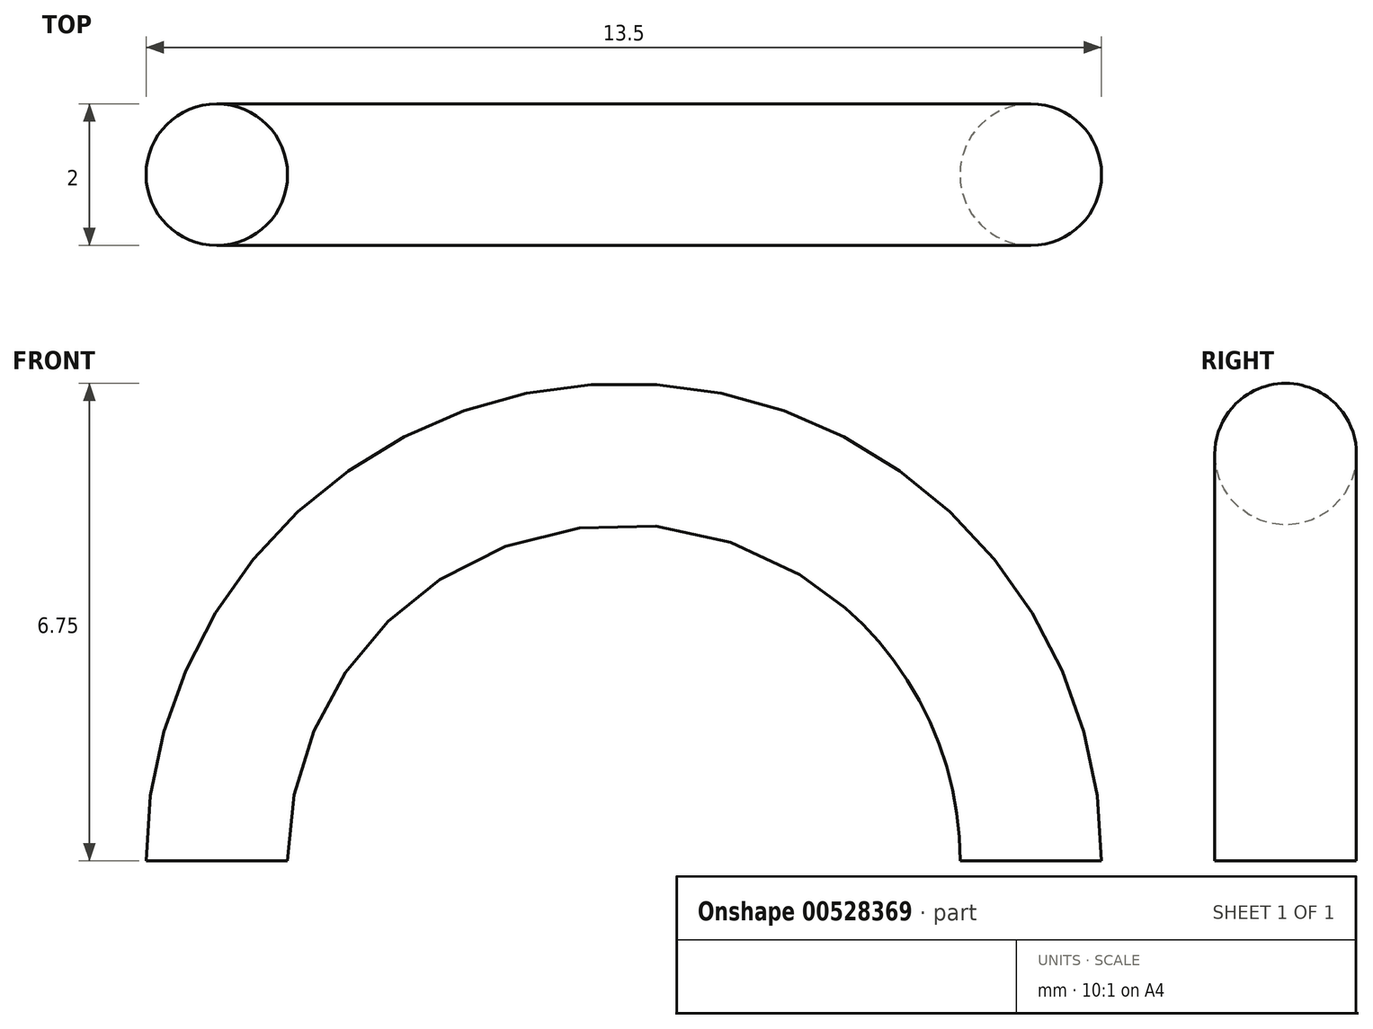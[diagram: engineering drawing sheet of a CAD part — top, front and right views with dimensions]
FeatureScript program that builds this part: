
annotation { "Feature Type Name" : "Feature", "Feature Type Description" : "" }
export const myFeature = defineFeature(function(context is Context, id is Id, definition is map)
    precondition{}
    {
        {
            var Q0;
            Q0=qCreatedBy(makeId("Front.planeOp"),FACE);
            var sketch = newSketch(context, id + "F0", { "sketchPlane" : qUnion([Q0])});
            skArc(sketch, "E0", {"start": v(11.5, 0) * mm, "mid": v(5.75, 5.75) * mm, "end": v(0, 0) * mm});
            skSolve(sketch);
        }
        {
            var Q0;
            Q0=sQuery(id+"F0.wireOp",EDGE,"E0");
            var Q1;
            Q1=sQuery(id+"F0.wireOp",VERTEX,"E0.start");
            cPlane(context, id + "F1", {"entities" : qUnion([Q0, Q1]), "cplaneType" : CPlaneType.CURVE_POINT, "offset" : 25.4 * mm, "width" : 152.4 * mm, "height" : 152.4 * mm});
        }
        {
            var Q0;
            Q0=qCreatedBy(id+"F1.planeOp",FACE);
            var sketch = newSketch(context, id + "F2", { "sketchPlane" : qUnion([Q0])});
            skCircle(sketch, "E1", {"center": v(11.5, 0) * mm, "radius": 1 * mm});
            skSolve(sketch);
        }
        {
            var Q0;
            Q0=makeQuery(id+"F2.imprint","IMPRINT",FACE,{"disambiguationData":[TD([[makeQuery(id+"F2.imprint","IMPRINT",EDGE,{"derivedFrom":sQuery(id+"F2.wireOp",EDGE,"E1")}),1.0]])]});
            var Q1;
            Q1=sQuery(id+"F0.wireOp",EDGE,"E0");
            sweep(context, id + "F3", {"profiles" : qUnion([Q0]), "path" : qUnion([Q1])});
        }
    });
